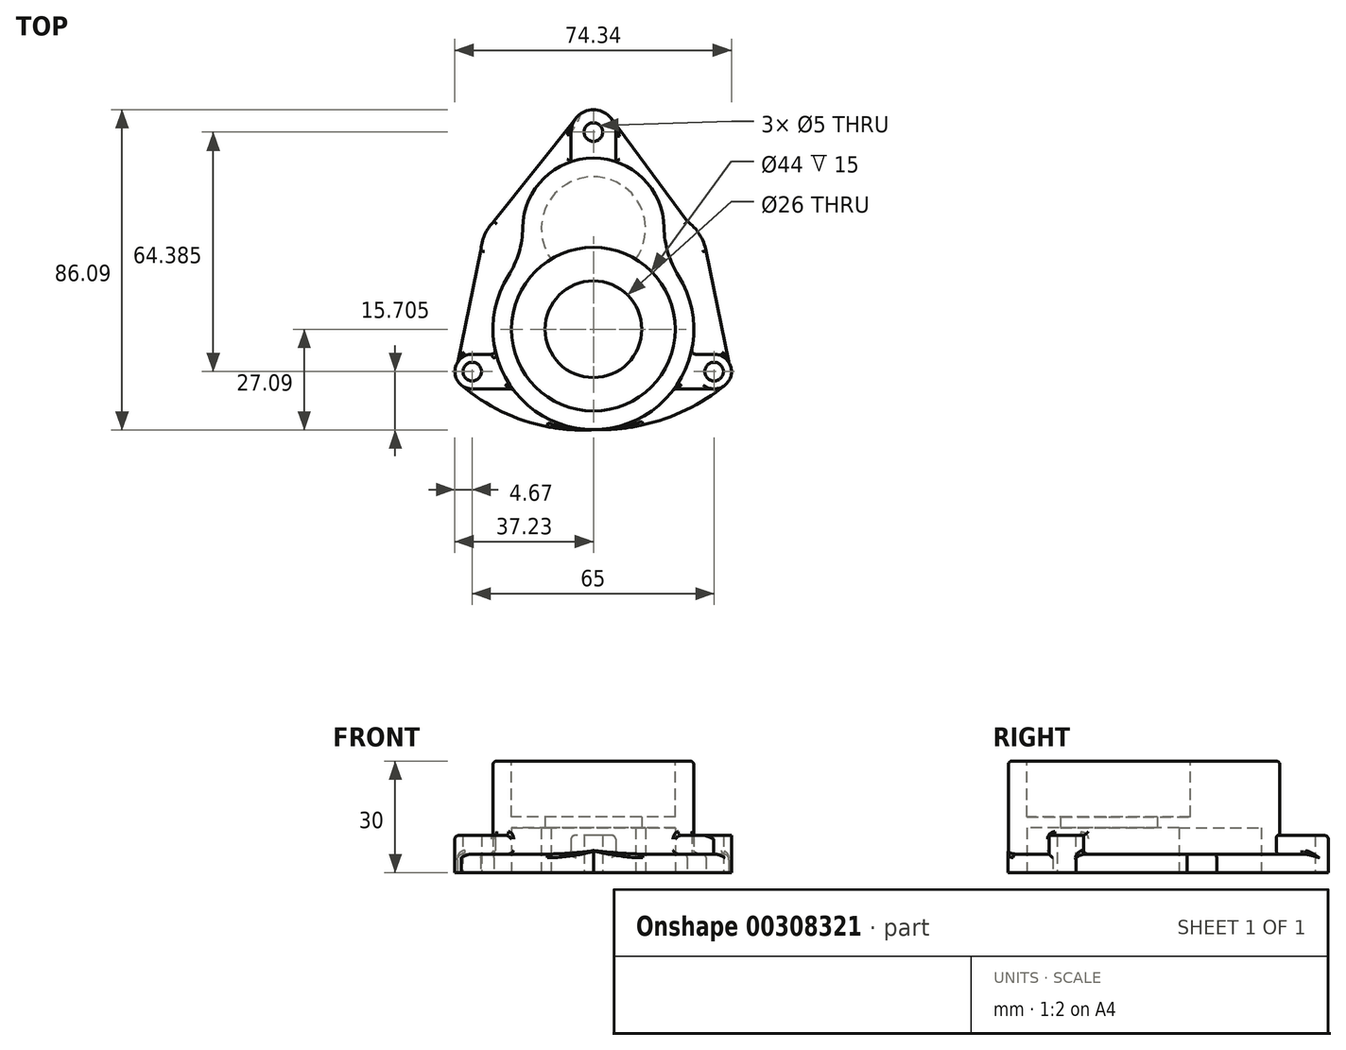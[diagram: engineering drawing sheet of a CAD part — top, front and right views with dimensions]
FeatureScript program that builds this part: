
annotation { "Feature Type Name" : "Feature", "Feature Type Description" : "" }
export const myFeature = defineFeature(function(context is Context, id is Id, definition is map)
    precondition{}
    {
        {
            var Q0;
            Q0=qCreatedBy(makeId("Top.planeOp"),FACE);
            var sketch = newSketch(context, id + "F0", { "sketchPlane" : qUnion([Q0])});
            skCircle(sketch, "E0", {"center": v(0, 0) * mm, "radius": 13 * mm});
            skCircle(sketch, "E1", {"center": v(0, 0) * mm, "radius": 22 * mm});
            skCircle(sketch, "E2", {"center": v(0, 0) * mm, "radius": 27 * mm});
            skCircle(sketch, "E3", {"center": v(0, 27) * mm, "radius": 14 * mm});
            skArc(sketch, "E4", {"start": v(17.79, 20.31) * mm, "mid": v(0, 46) * mm, "end": v(-17.79, 20.31) * mm});
            skCircle(sketch, "E5", {"center": v(0, 53) * mm, "radius": 6 * mm});
            skPoint(sketch, "E5.centerSnap0", {"position": v(0, 46) * mm});
            skLineSegment(sketch, "E6", {"start": v(-6, 53) * mm, "end": v(-6, 45.03) * mm});
            skLineSegment(sketch, "E7", {"start": v(6, 53) * mm, "end": v(6, 45.03) * mm});
            skCircle(sketch, "E8", {"center": v(-32.56, -11.38) * mm, "radius": 4.67 * mm});
            skPoint(sketch, "E9.start.orphan", {"position": v(0, -12) * mm});
            skCircle(sketch, "E10", {"center": v(-32.56, -11.38) * mm, "radius": 2.5 * mm});
            skLineSegment(sketch, "E11", {"start": v(-32.56, -6.72) * mm, "end": v(-26.15, -6.72) * mm});
            skLineSegment(sketch, "E12", {"start": v(-32.56, -16.05) * mm, "end": v(-21.7, -16.05) * mm});
            skCircle(sketch, "E13", {"center": v(32.44, -11.38) * mm, "radius": 4.67 * mm});
            skLineSegment(sketch, "E14", {"start": v(32.44, -6.72) * mm, "end": v(26.15, -6.72) * mm});
            skPoint(sketch, "E14.startSnap0", {"position": v(-29.36, -6.72) * mm});
            skPoint(sketch, "E14.endSnap0", {"position": v(-29.36, -6.72) * mm});
            skLineSegment(sketch, "E15", {"start": v(32.32, -16.05) * mm, "end": v(21.71, -16.05) * mm});
            skCircle(sketch, "E16", {"center": v(32.44, -11.38) * mm, "radius": 2.5 * mm});
            skArc(sketch, "E17", {"start": v(-35.5, -15) * mm, "mid": v(-18.92, -24.46) * mm, "end": v(0, -27) * mm});
            skArc(sketch, "E18", {"start": v(0, -27) * mm, "mid": v(18.77, -24.19) * mm, "end": v(35.39, -15) * mm});
            skArc(sketch, "E19", {"start": v(-26.78, 29) * mm, "mid": v(-29.24, 25.33) * mm, "end": v(-30.26, 21.03) * mm});
            skLineSegment(sketch, "E20", {"start": v(-36.48, -8.84) * mm, "end": v(-30.26, 21.03) * mm});
            skLineSegment(sketch, "E21", {"start": v(-26.78, 29) * mm, "end": v(-4.7, 56.74) * mm});
            skLineSegment(sketch, "E22", {"start": v(25.2, 29) * mm, "end": v(4.7, 56.74) * mm});
            skLineSegment(sketch, "E23", {"start": v(30.26, 21.03) * mm, "end": v(36.36, -8.84) * mm});
            skArc(sketch, "E24.trimOffspring", {"start": v(30.26, 21.03) * mm, "mid": v(28.51, 25.51) * mm, "end": v(25.2, 29) * mm});
            skCircle(sketch, "E25", {"center": v(0, 53) * mm, "radius": 2.5 * mm});
            skPoint(sketch, "E26.start.orphan", {"position": v(0, 28) * mm});
            skSolve(sketch);
        }
        {
            var Q0;
            {var subQ0=sQuery(id+"F0.wireOp",EDGE,"E4");var subQ1=sQuery(id+"F0.wireOp",EDGE,"E2");var subQ2=makeQuery(id+"F0.imprint","INTERSECT",VERTEX,{"disambiguationData":[OD(0.0)],"derivedFrom":[subQ1,subQ0]});Q0=makeQuery(id+"F0.imprint","IMPRINT",FACE,{"disambiguationData":[TD([[makeQuery(id+"F0.imprint","IMPRINT",EDGE,{"disambiguationData":[TD([[subQ2,-1.0]])],"derivedFrom":subQ1}),-1.0]])]});}
            var Q1;
            {var subQ0=sQuery(id+"F0.wireOp",EDGE,"E3");var subQ1=sQuery(id+"F0.wireOp",EDGE,"E1");var subQ2=makeQuery(id+"F0.imprint","INTERSECT",VERTEX,{"disambiguationData":[OD(0.0)],"derivedFrom":[subQ1,subQ0]});Q1=makeQuery(id+"F0.imprint","IMPRINT",FACE,{"disambiguationData":[TD([[makeQuery(id+"F0.imprint","IMPRINT",EDGE,{"disambiguationData":[TD([[subQ2,-1.0]])],"derivedFrom":subQ1}),-1.0]])]});}
            var Q2;
            {var subQ0=sQuery(id+"F0.wireOp",EDGE,"E3");var subQ1=sQuery(id+"F0.wireOp",EDGE,"E2");var subQ2=makeQuery(id+"F0.imprint","INTERSECT",VERTEX,{"disambiguationData":[OD(0.0)],"derivedFrom":[subQ1,subQ0]});Q2=makeQuery(id+"F0.imprint","IMPRINT",FACE,{"disambiguationData":[TD([[makeQuery(id+"F0.imprint","IMPRINT",EDGE,{"disambiguationData":[TD([[subQ2,-1.0]])],"derivedFrom":subQ1}),-1.0]])]});}
            var Q3;
            {var subQ0=sQuery(id+"F0.wireOp",EDGE,"E3");var subQ1=sQuery(id+"F0.wireOp",EDGE,"E1");var subQ2=makeQuery(id+"F0.imprint","INTERSECT",VERTEX,{"disambiguationData":[OD(0.0)],"derivedFrom":[subQ1,subQ0]});Q3=makeQuery(id+"F0.imprint","IMPRINT",FACE,{"disambiguationData":[TD([[makeQuery(id+"F0.imprint","IMPRINT",EDGE,{"disambiguationData":[TD([[subQ2,1.0]])],"derivedFrom":subQ1}),-1.0]])]});}
            var Q4;
            {var subQ0=sQuery(id+"F0.wireOp",EDGE,"E3");var subQ1=sQuery(id+"F0.wireOp",EDGE,"E1");var subQ2=makeQuery(id+"F0.imprint","INTERSECT",VERTEX,{"disambiguationData":[OD(0.0)],"derivedFrom":[subQ1,subQ0]});Q4=makeQuery(id+"F0.imprint","IMPRINT",FACE,{"disambiguationData":[TD([[makeQuery(id+"F0.imprint","IMPRINT",EDGE,{"disambiguationData":[TD([[subQ2,1.0]])],"derivedFrom":subQ1}),1.0]])]});}
            var Q5;
            Q5=makeQuery(id+"F0.imprint","IMPRINT",FACE,{"disambiguationData":[TD([[makeQuery(id+"F0.imprint","IMPRINT",EDGE,{"derivedFrom":sQuery(id+"F0.wireOp",EDGE,"E0")}),1.0]])]});
            var Q6;
            {var subQ0=sQuery(id+"F0.wireOp",EDGE,"E0");Q6=makeQuery(id+"F0.imprint","IMPRINT",FACE,{"disambiguationData":[TD([[makeQuery(id+"F0.imprint","IMPRINT",EDGE,{"derivedFrom":subQ0}),-1.0]])]});}
            extrude(context, id + "F1", {"entities" : qUnion([Q0, Q1, Q2, Q3, Q4, Q5, Q6]), "depth" : 30 * mm});
        }
        {
            var Q0;
            {var subQ0=sQuery(id+"F0.wireOp",EDGE,"E4");var subQ1=sQuery(id+"F0.wireOp",EDGE,"E2");Q0=makeQuery(id+"F1.opExtrude","SWEPT_EDGE",EDGE,{"disambiguationData":[OSD([subQ1,subQ0]),TDD([makeQuery(id+"F0.imprint","INTERSECT",VERTEX,{"disambiguationData":[OD(1.0)],"derivedFrom":[subQ1,subQ0]})])]});}
            var Q1;
            {var subQ0=sQuery(id+"F0.wireOp",EDGE,"E4");var subQ1=sQuery(id+"F0.wireOp",EDGE,"E2");Q1=makeQuery(id+"F1.opExtrude","SWEPT_EDGE",EDGE,{"disambiguationData":[OSD([subQ1,subQ0]),TDD([makeQuery(id+"F0.imprint","INTERSECT",VERTEX,{"disambiguationData":[OD(0.0)],"derivedFrom":[subQ1,subQ0]})])]});}
            fillet(context, id + "F2", {"entities" : qUnion([Q0, Q1]), "radius" : 25 * mm, "tangentPropagation" : true, "allowEdgeOverflow" : false});
        }
        {
            var Q0;
            {var subQ0=sQuery(id+"F0.wireOp",EDGE,"E6");Q0=makeQuery(id+"F0.imprint","IMPRINT",FACE,{"disambiguationData":[TD([[makeQuery(id+"F0.imprint","IMPRINT",EDGE,{"derivedFrom":subQ0}),1.0]])]});}
            var Q1;
            Q1=makeQuery(id+"F0.imprint","IMPRINT",FACE,{"disambiguationData":[TD([[makeQuery(id+"F0.imprint","IMPRINT",EDGE,{"derivedFrom":sQuery(id+"F0.wireOp",EDGE,"E25")}),-1.0]])]});
            var Q2;
            Q2=makeQuery(id+"F0.imprint","IMPRINT",FACE,{"disambiguationData":[TD([[makeQuery(id+"F0.imprint","IMPRINT",EDGE,{"derivedFrom":sQuery(id+"F0.wireOp",EDGE,"E16")}),-1.0]])]});
            var Q3;
            {var subQ0=sQuery(id+"F0.wireOp",EDGE,"E14");Q3=makeQuery(id+"F0.imprint","IMPRINT",FACE,{"disambiguationData":[TD([[makeQuery(id+"F0.imprint","IMPRINT",EDGE,{"derivedFrom":subQ0}),1.0]])]});}
            var Q4;
            {var subQ0=sQuery(id+"F0.wireOp",EDGE,"E11");Q4=makeQuery(id+"F0.imprint","IMPRINT",FACE,{"disambiguationData":[TD([[makeQuery(id+"F0.imprint","IMPRINT",EDGE,{"derivedFrom":subQ0}),-1.0]])]});}
            var Q5;
            Q5=makeQuery(id+"F0.imprint","IMPRINT",FACE,{"disambiguationData":[TD([[makeQuery(id+"F0.imprint","IMPRINT",EDGE,{"derivedFrom":sQuery(id+"F0.wireOp",EDGE,"E10")}),-1.0]])]});
            extrude(context, id + "F3", {"entities" : qUnion([Q0, Q1, Q2, Q3, Q4, Q5]), "operationType" : NewBodyOperationType.ADD, "depth" : 10 * mm});
        }
        {
            var Q0;
            {var subQ0=sQuery(id+"F0.wireOp",EDGE,"E6");Q0=makeQuery(id+"F0.imprint","IMPRINT",FACE,{"disambiguationData":[TD([[makeQuery(id+"F0.imprint","IMPRINT",EDGE,{"derivedFrom":subQ0}),-1.0]])]});}
            var Q1;
            {var subQ0=sQuery(id+"F0.wireOp",EDGE,"E7");Q1=makeQuery(id+"F0.imprint","IMPRINT",FACE,{"disambiguationData":[TD([[makeQuery(id+"F0.imprint","IMPRINT",EDGE,{"derivedFrom":subQ0}),1.0]])]});}
            var Q2;
            {var subQ0=sQuery(id+"F0.wireOp",EDGE,"E12");Q2=makeQuery(id+"F0.imprint","IMPRINT",FACE,{"disambiguationData":[TD([[makeQuery(id+"F0.imprint","IMPRINT",EDGE,{"derivedFrom":subQ0}),-1.0]])]});}
            var Q3;
            {var subQ0=sQuery(id+"F0.wireOp",EDGE,"E15");Q3=makeQuery(id+"F0.imprint","IMPRINT",FACE,{"disambiguationData":[TD([[makeQuery(id+"F0.imprint","IMPRINT",EDGE,{"derivedFrom":subQ0}),1.0]])]});}
            extrude(context, id + "F4", {"entities" : qUnion([Q0, Q1, Q2, Q3]), "operationType" : NewBodyOperationType.ADD, "depth" : 5 * mm});
        }
        {
            var Q0;
            {var subQ0=sQuery(id+"F0.wireOp",EDGE,"E0");Q0=makeQuery(id+"F0.imprint","IMPRINT",FACE,{"disambiguationData":[TD([[makeQuery(id+"F0.imprint","IMPRINT",EDGE,{"derivedFrom":subQ0}),-1.0]])]});}
            var Q1;
            Q1=makeQuery(id+"F0.imprint","IMPRINT",FACE,{"disambiguationData":[TD([[makeQuery(id+"F0.imprint","IMPRINT",EDGE,{"derivedFrom":sQuery(id+"F0.wireOp",EDGE,"E0")}),1.0]])]});
            var Q2;
            {var subQ0=sQuery(id+"F0.wireOp",EDGE,"E3");var subQ1=sQuery(id+"F0.wireOp",EDGE,"E1");var subQ2=makeQuery(id+"F0.imprint","INTERSECT",VERTEX,{"disambiguationData":[OD(0.0)],"derivedFrom":[subQ1,subQ0]});Q2=makeQuery(id+"F0.imprint","IMPRINT",FACE,{"disambiguationData":[TD([[makeQuery(id+"F0.imprint","IMPRINT",EDGE,{"disambiguationData":[TD([[subQ2,1.0]])],"derivedFrom":subQ1}),1.0]])]});}
            var Q3;
            {var subQ0=sQuery(id+"F0.wireOp",EDGE,"E3");var subQ1=sQuery(id+"F0.wireOp",EDGE,"E1");var subQ2=makeQuery(id+"F0.imprint","INTERSECT",VERTEX,{"disambiguationData":[OD(0.0)],"derivedFrom":[subQ1,subQ0]});Q3=makeQuery(id+"F0.imprint","IMPRINT",FACE,{"disambiguationData":[TD([[makeQuery(id+"F0.imprint","IMPRINT",EDGE,{"disambiguationData":[TD([[subQ2,1.0]])],"derivedFrom":subQ1}),-1.0]])]});}
            var Q4;
            {var subQ0=sQuery(id+"F0.wireOp",EDGE,"E3");var subQ1=sQuery(id+"F0.wireOp",EDGE,"E2");var subQ2=makeQuery(id+"F0.imprint","INTERSECT",VERTEX,{"disambiguationData":[OD(0.0)],"derivedFrom":[subQ1,subQ0]});Q4=makeQuery(id+"F0.imprint","IMPRINT",FACE,{"disambiguationData":[TD([[makeQuery(id+"F0.imprint","IMPRINT",EDGE,{"disambiguationData":[TD([[subQ2,-1.0]])],"derivedFrom":subQ1}),-1.0]])]});}
            extrude(context, id + "F5", {"entities" : qUnion([Q0, Q1, Q2, Q3, Q4]), "operationType" : NewBodyOperationType.REMOVE, "depth" : 12 * mm});
        }
        {
            var Q0;
            Q0=makeQuery(id+"F1.opExtrude","CAP_FACE",FACE,{"disambiguationData":[OSD([sQuery(id+"F0.wireOp",EDGE,"E2"),sQuery(id+"F0.wireOp",EDGE,"E4")])],"isStart":false});
            var sketch = newSketch(context, id + "F6", { "sketchPlane" : qUnion([Q0])});
            skCircle(sketch, "E27.0", {"center": v(0, 0) * mm, "radius": 22 * mm});
            skSolve(sketch);
        }
        {
            var Q0;
            Q0 = qSketchRegion(id + "F6", true);
            extrude(context, id + "F7", {"entities" : qUnion([Q0]), "operationType" : NewBodyOperationType.REMOVE, "oppositeDirection" : true, "depth" : 15 * mm});
        }
        {
            var Q0;
            Q0=makeQuery(id+"F0.imprint","IMPRINT",FACE,{"disambiguationData":[TD([[makeQuery(id+"F0.imprint","IMPRINT",EDGE,{"derivedFrom":sQuery(id+"F0.wireOp",EDGE,"E0")}),1.0]])]});
            extrude(context, id + "F8", {"entities" : qUnion([Q0]), "operationType" : NewBodyOperationType.REMOVE, "endBound" : BoundingType.THROUGH_ALL, "depth" : 25 * mm});
        }
        {
            var Q0;
            Q0=makeQuery(id+"F1.opExtrude","SWEPT_FACE",FACE,{"disambiguationData":[OSD([sQuery(id+"F0.wireOp",EDGE,"E2")])]});
            var Q1;
            Q1=makeQuery(id+"F4.opExtrude","CAP_FACE",FACE,{"disambiguationData":[OSD([sQuery(id+"F0.wireOp",EDGE,"E2"),sQuery(id+"F0.wireOp",EDGE,"E4"),sQuery(id+"F0.wireOp",EDGE,"E5"),sQuery(id+"F0.wireOp",EDGE,"E7"),sQuery(id+"F0.wireOp",EDGE,"E13"),sQuery(id+"F0.wireOp",EDGE,"E14"),sQuery(id+"F0.wireOp",EDGE,"E22"),sQuery(id+"F0.wireOp",EDGE,"E23"),sQuery(id+"F0.wireOp",EDGE,"E24.trimOffspring")])],"isStart":false});
            var Q2;
            Q2=makeQuery(id+"F3.opExtrude","CAP_EDGE",EDGE,{"disambiguationData":[OSD([sQuery(id+"F0.wireOp",EDGE,"E7")])],"isStart":false});
            var Q3;
            Q3=makeQuery(id+"F4.opExtrude","CAP_FACE",FACE,{"disambiguationData":[OSD([sQuery(id+"F0.wireOp",EDGE,"E2"),sQuery(id+"F0.wireOp",EDGE,"E4"),sQuery(id+"F0.wireOp",EDGE,"E5"),sQuery(id+"F0.wireOp",EDGE,"E6"),sQuery(id+"F0.wireOp",EDGE,"E8"),sQuery(id+"F0.wireOp",EDGE,"E11"),sQuery(id+"F0.wireOp",EDGE,"E19"),sQuery(id+"F0.wireOp",EDGE,"E20"),sQuery(id+"F0.wireOp",EDGE,"E21")])],"isStart":false});
            var Q4;
            Q4=makeQuery(id+"F3.opExtrude","CAP_EDGE",EDGE,{"disambiguationData":[OSD([sQuery(id+"F0.wireOp",EDGE,"E15")])],"isStart":false});
            var Q5;
            Q5=makeQuery(id+"F3.opExtrude","CAP_EDGE",EDGE,{"disambiguationData":[OSD([sQuery(id+"F0.wireOp",EDGE,"E12")])],"isStart":false});
            var Q6;
            Q6=makeQuery(id+"F4.opExtrude","CAP_EDGE",EDGE,{"disambiguationData":[OSD([sQuery(id+"F0.wireOp",EDGE,"E12")])],"isStart":false});
            fillet(context, id + "F9", {"entities" : qUnion([Q0, Q1, Q2, Q3, Q4, Q5, Q6]), "radius" : 1 * mm, "tangentPropagation" : true, "allowEdgeOverflow" : false});
        }
        {
            var Q0;
            Q0=makeQuery(id+"F4.opExtrude","CAP_EDGE",EDGE,{"disambiguationData":[OSD([sQuery(id+"F0.wireOp",EDGE,"E17")])],"isStart":false});
            var Q1;
            Q1=makeQuery(id+"F4.opExtrude","CAP_EDGE",EDGE,{"disambiguationData":[OSD([sQuery(id+"F0.wireOp",EDGE,"E18")])],"isStart":false});
            fillet(context, id + "F10", {"entities" : qUnion([Q0, Q1]), "radius" : 1 * mm, "tangentPropagation" : true, "allowEdgeOverflow" : false});
        }
    });
